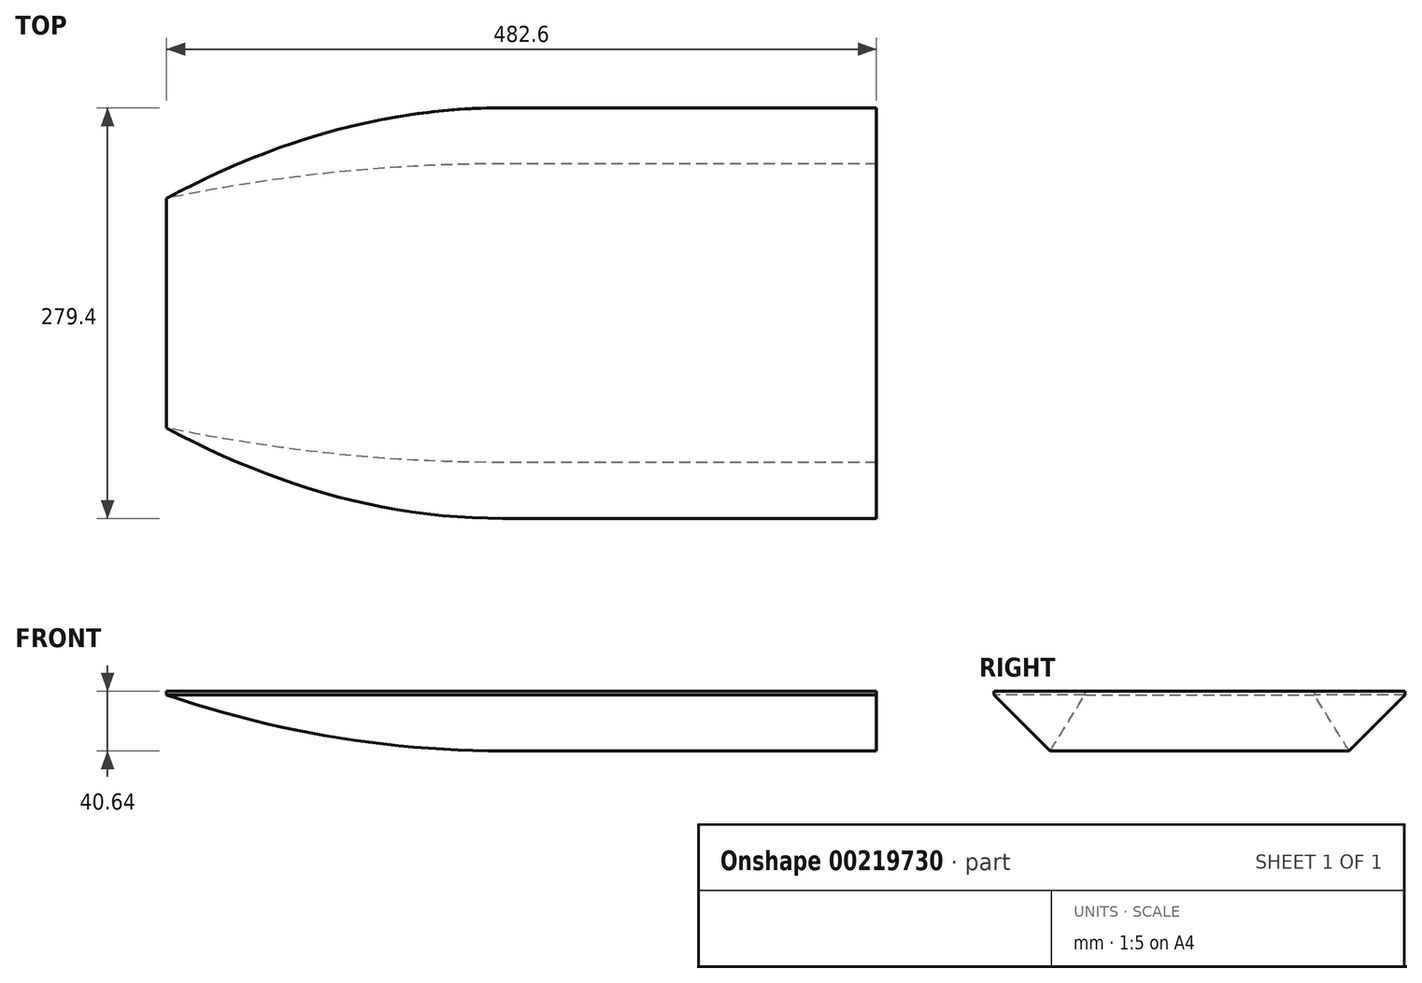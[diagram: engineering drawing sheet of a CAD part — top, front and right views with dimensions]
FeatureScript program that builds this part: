
annotation { "Feature Type Name" : "Feature", "Feature Type Description" : "" }
export const myFeature = defineFeature(function(context is Context, id is Id, definition is map)
    precondition{}
    {
        {
            var Q0;
            Q0=qCreatedBy(makeId("Front.planeOp"),FACE);
            var sketch = newSketch(context, id + "F0", { "sketchPlane" : qUnion([Q0])});
            skLineSegment(sketch, "E0.bottom", {"start": v(0, 0) * mm, "end": v(254, 0) * mm});
            skLineSegment(sketch, "E0.right", {"start": v(254, 0) * mm, "end": v(254, 38.1) * mm});
            skLineSegment(sketch, "E1", {"start": v(254, 38.1) * mm, "end": v(-228.6, 38.1) * mm});
            skArc(sketch, "E2", {"start": v(0, 0) * mm, "mid": v(-115.88, 9.6) * mm, "end": v(-228.6, 38.1) * mm});
            skSolve(sketch);
        }
        {
            var Q0;
            Q0=makeQuery(id+"F0.imprint","IMPRINT",FACE,{"disambiguationData":[TD([[makeQuery(id+"F0.imprint","IMPRINT",EDGE,{"derivedFrom":sQuery(id+"F0.wireOp",EDGE,"E0.bottom")}),1.0]])]});
            extrude(context, id + "F1", {"entities" : qUnion([Q0]), "depth" : 88.9 * mm});
        }
        {
            var Q0;
            Q0=makeQuery(id+"F1.opExtrude","CAP_FACE",FACE,{"disambiguationData":[OSD([sQuery(id+"F0.wireOp",EDGE,"E0.bottom"),sQuery(id+"F0.wireOp",EDGE,"E0.right"),sQuery(id+"F0.wireOp",EDGE,"E1"),sQuery(id+"F0.wireOp",EDGE,"E2")])],"isStart":false});
            extrude(context, id + "F2", {"entities" : qUnion([Q0]), "operationType" : NewBodyOperationType.ADD, "depth" : 50.8 * mm});
        }
        {
            var Q0;
            {var subQ0=sQuery(id+"F0.wireOp",EDGE,"E1");Q0=makeQuery(id+"F2.boolean.opBoolean","MERGE",FACE,{"derivedFrom":[makeQuery(id+"F1.opExtrude","SWEPT_FACE",FACE,{"disambiguationData":[OSD([subQ0])]}),makeQuery(id+"F2.opExtrude","SWEPT_FACE",FACE,{"disambiguationData":[OSD([subQ0])]})]});}
            var sketch = newSketch(context, id + "F3", { "sketchPlane" : qUnion([Q0])});
            skLineSegment(sketch, "E3", {"start": v(-304.42, -139.7) * mm, "end": v(0, -139.7) * mm});
            skArc(sketch, "E4", {"start": v(-228.6, -114.3) * mm, "mid": v(-115, -133.33) * mm, "end": v(0, -139.7) * mm});
            skLineSegment(sketch, "E5", {"start": v(-304.42, -139.7) * mm, "end": v(-304.42, -114.3) * mm});
            skLineSegment(sketch, "E6", {"start": v(-304.42, -114.3) * mm, "end": v(-228.6, -114.3) * mm});
            skSolve(sketch);
        }
        {
            var Q0;
            Q0=qSketchRegion(id+"F3",true);
            extrude(context, id + "F4", {"entities" : qUnion([Q0]), "operationType" : NewBodyOperationType.REMOVE, "endBound" : BoundingType.THROUGH_ALL, "oppositeDirection" : true, "depth" : 25.4 * mm});
        }
        {
            var Q0;
            Q0=makeQuery(id+"F2.opExtrude","CAP_EDGE",EDGE,{"disambiguationData":[OSD([sQuery(id+"F0.wireOp",EDGE,"E0.bottom")])],"isStart":false});
            chamfer(context, id + "F5", {"entities" : qUnion([Q0]), "width" : 38.1 * mm, "tangentPropagation" : true});
        }
        {
            var Q0;
            Q0=makeQuery(id+"F1.opExtrude","SWEPT_BODY",BODY,{"disambiguationData":[OSD([sQuery(id+"F0.wireOp",EDGE,"E0.bottom"),sQuery(id+"F0.wireOp",EDGE,"E0.right"),sQuery(id+"F0.wireOp",EDGE,"E1"),sQuery(id+"F0.wireOp",EDGE,"E2")])]});
            var Q1;
            Q1=qCreatedBy(makeId("Front.planeOp"),FACE);
            mirror(context, id + "F6", {"operationType" : NewBodyOperationType.ADD, "entities" : qUnion([Q0]), "mirrorPlane" : qUnion([Q1])});
        }
        {
            var Q0;
            {var subQ0=sQuery(id+"F0.wireOp",EDGE,"E1");var subQ1=makeQuery(id+"F2.boolean.opBoolean","MERGE",FACE,{"derivedFrom":[makeQuery(id+"F1.opExtrude","SWEPT_FACE",FACE,{"disambiguationData":[OSD([subQ0])]}),makeQuery(id+"F2.opExtrude","SWEPT_FACE",FACE,{"disambiguationData":[OSD([subQ0])]})]});Q0=makeQuery(id+"F6.boolean.opBoolean","MERGE",FACE,{"derivedFrom":[subQ1,makeQuery(id+"F6.opPattern","COPY",FACE,{"derivedFrom":subQ1,"instanceName":"1"})]});}
            extrude(context, id + "F7", {"entities" : qUnion([Q0]), "operationType" : NewBodyOperationType.ADD, "depth" : 2.54 * mm});
        }
        {
            var Q0;
            Q0=qCreatedBy(makeId("Right.planeOp"),FACE);
            cPlane(context, id + "F8", {"entities" : qUnion([Q0]), "cplaneType" : CPlaneType.OFFSET, "offset" : 25.4 * mm, "width" : 152.4 * mm, "height" : 152.4 * mm});
        }
    });
